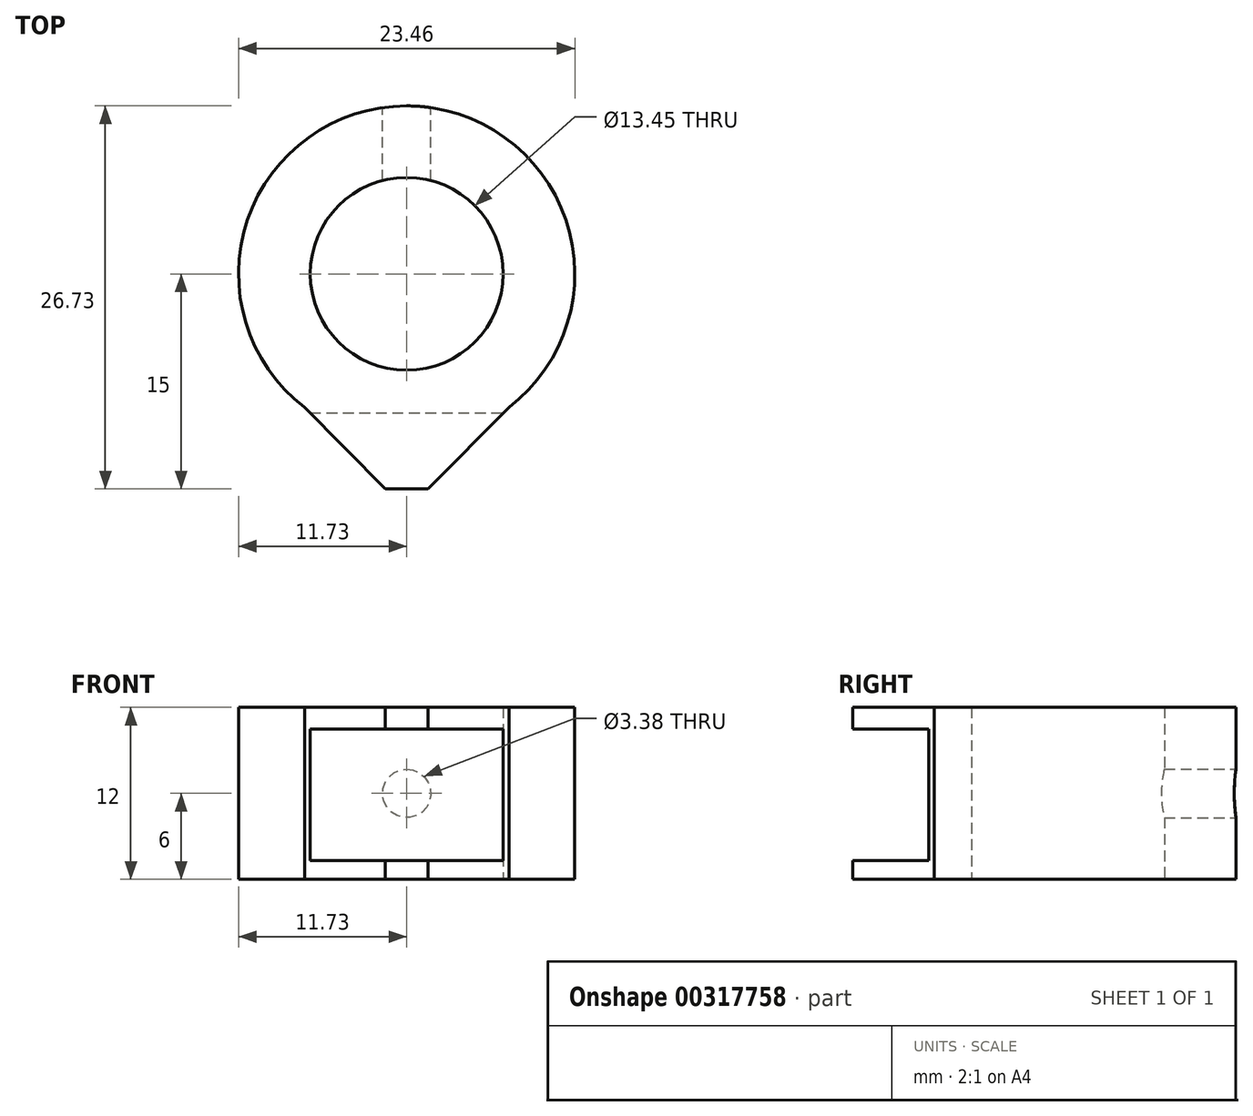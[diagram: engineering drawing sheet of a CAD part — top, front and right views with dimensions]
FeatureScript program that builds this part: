
annotation { "Feature Type Name" : "Feature", "Feature Type Description" : "" }
export const myFeature = defineFeature(function(context is Context, id is Id, definition is map)
    precondition{}
    {
        {
            var Q0;
            Q0=qCreatedBy(makeId("Top.planeOp"),FACE);
            var sketch = newSketch(context, id + "F0", { "sketchPlane" : qUnion([Q0])});
            skCircle(sketch, "E0", {"center": v(0, 0) * mm, "radius": 6.72 * mm});
            skLineSegment(sketch, "E1", {"start": v(-20.81, 0) * mm, "end": v(24.73, 0) * mm, "construction": true});
            skLineSegment(sketch, "E2", {"start": v(0, 0) * mm, "end": v(0, -15) * mm, "construction": true});
            skCircle(sketch, "E3.0", {"center": v(0, 0) * mm, "radius": 11.72 * mm});
            skLineSegment(sketch, "E4", {"start": v(-7.13, -9.31) * mm, "end": v(-1.5, -15) * mm});
            skLineSegment(sketch, "E5", {"start": v(-1.5, -15) * mm, "end": v(0, -15) * mm});
            skLineSegment(sketch, "E6.MirrorCS", {"start": v(1.5, -15) * mm, "end": v(0, -15) * mm});
            skLineSegment(sketch, "E7.MirrorCS", {"start": v(7.13, -9.31) * mm, "end": v(1.5, -15) * mm});
            skSolve(sketch);
        }
        {
            var Q0;
            Q0=qSketchRegion(id+"F0",true);
            extrude(context, id + "F1", {"entities" : qUnion([Q0]), "depth" : 12 * mm});
        }
        {
            var Q0;
            Q0=makeQuery(id+"F1.opExtrude","SWEPT_FACE",FACE,{"disambiguationData":[OSD([sQuery(id+"F0.wireOp",EDGE,"E5"),sQuery(id+"F0.wireOp",EDGE,"E6.MirrorCS")])]});
            cPlane(context, id + "F2", {"entities" : qUnion([Q0]), "cplaneType" : CPlaneType.OFFSET, "offset" : 27 * mm, "oppositeDirection" : true, "width" : 150 * mm, "height" : 150 * mm});
        }
        {
            var Q0;
            Q0=qCreatedBy(id+"F2.planeOp",FACE);
            var sketch = newSketch(context, id + "F3", { "sketchPlane" : qUnion([Q0])});
            skLineSegment(sketch, "E8", {"start": v(0, 0) * mm, "end": v(0, 12) * mm});
            skCircle(sketch, "E9", {"center": v(0, 6) * mm, "radius": 1.69 * mm});
            skSolve(sketch);
        }
        {
            var Q0;
            Q0=qSketchRegion(id+"F3",true);
            extrude(context, id + "F4", {"entities" : qUnion([Q0]), "operationType" : NewBodyOperationType.REMOVE, "depth" : 10 * mm});
        }
        {
            var Q0;
            Q0=makeQuery(id+"F1.opExtrude","SWEPT_FACE",FACE,{"disambiguationData":[OSD([sQuery(id+"F0.wireOp",EDGE,"E5"),sQuery(id+"F0.wireOp",EDGE,"E6.MirrorCS")])]});
            var sketch = newSketch(context, id + "F5", { "sketchPlane" : qUnion([Q0])});
            skLineSegment(sketch, "E10", {"start": v(-1.5, 10.5) * mm, "end": v(1.5, 10.5) * mm});
            skLineSegment(sketch, "E11", {"start": v(1.5, 10.5) * mm, "end": v(1.5, 1.3) * mm});
            skLineSegment(sketch, "E12", {"start": v(1.5, 1.3) * mm, "end": v(-1.5, 1.3) * mm});
            skLineSegment(sketch, "E13", {"start": v(-1.5, 1.3) * mm, "end": v(-1.5, 10.5) * mm});
            skLineSegment(sketch, "E14", {"start": v(-1.5, 10.5) * mm, "end": v(-8.13, 10.5) * mm});
            skLineSegment(sketch, "E15", {"start": v(-8.13, 10.5) * mm, "end": v(-8.13, 1.3) * mm});
            skLineSegment(sketch, "E16", {"start": v(-8.13, 1.3) * mm, "end": v(-1.5, 1.3) * mm});
            skLineSegment(sketch, "E17", {"start": v(0, 10.5) * mm, "end": v(0, 1.3) * mm, "construction": true});
            skLineSegment(sketch, "E18.MirrorCS", {"start": v(1.5, 10.5) * mm, "end": v(8.13, 10.5) * mm});
            skLineSegment(sketch, "E19.MirrorCS", {"start": v(8.13, 10.5) * mm, "end": v(8.13, 1.3) * mm});
            skLineSegment(sketch, "E20.MirrorCS", {"start": v(8.13, 1.3) * mm, "end": v(1.5, 1.3) * mm});
            skSolve(sketch);
        }
        {
            var Q0;
            Q0 = qSketchRegion(id + "F5", true);
            extrude(context, id + "F6", {"entities" : qUnion([Q0]), "operationType" : NewBodyOperationType.REMOVE, "oppositeDirection" : true, "depth" : 5.3 * mm});
        }
    });
